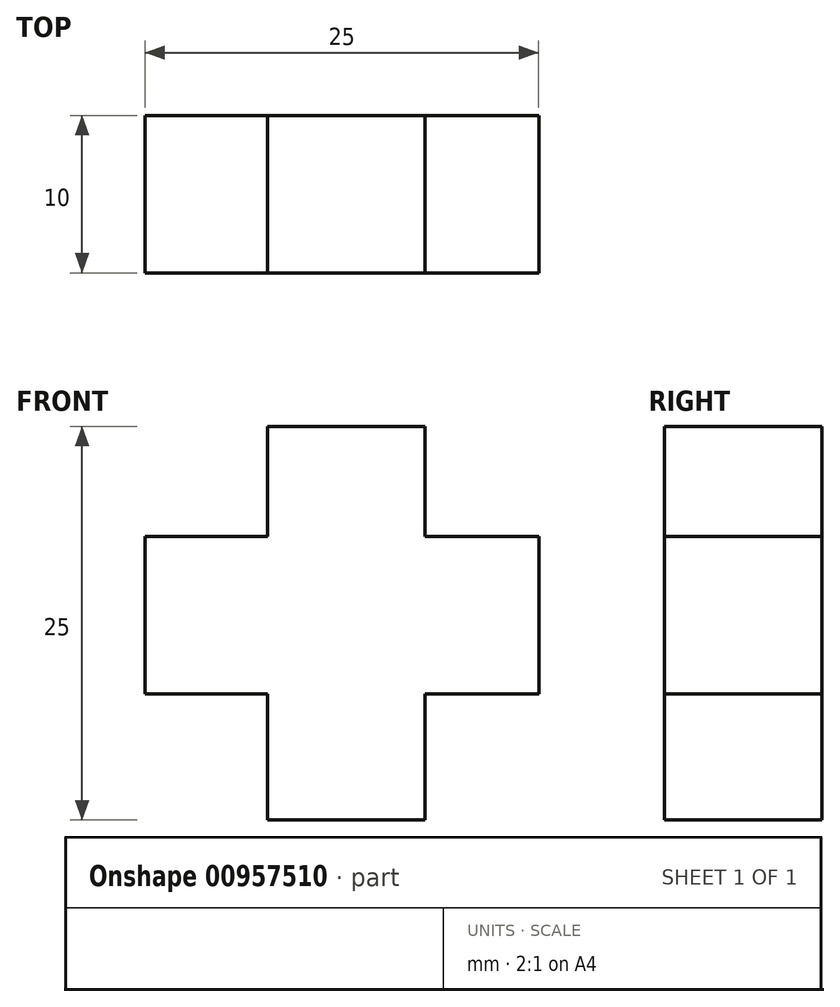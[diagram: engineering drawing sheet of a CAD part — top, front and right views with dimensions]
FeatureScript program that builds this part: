
annotation { "Feature Type Name" : "Feature", "Feature Type Description" : "" }
export const myFeature = defineFeature(function(context is Context, id is Id, definition is map)
    precondition{}
    {
        {
            var Q0;
            Q0=qCreatedBy(makeId("Front.planeOp"),FACE);
            var sketch = newSketch(context, id + "F0", { "sketchPlane" : qUnion([Q0])});
            skLineSegment(sketch, "E0.bottom", {"start": v(-11.23, 5.5) * mm, "end": v(13.77, 5.5) * mm});
            skLineSegment(sketch, "E0.top", {"start": v(-11.23, -4.5) * mm, "end": v(13.77, -4.5) * mm});
            skLineSegment(sketch, "E0.left", {"start": v(-11.23, 5.5) * mm, "end": v(-11.23, -4.5) * mm});
            skLineSegment(sketch, "E0.right", {"start": v(13.77, 5.5) * mm, "end": v(13.77, -4.5) * mm});
            skLineSegment(sketch, "E1", {"start": v(-11.23, -4.5) * mm, "end": v(-11.29, 0.5) * mm});
            skLineSegment(sketch, "E2.bottom", {"start": v(-3.46, 12.5) * mm, "end": v(6.54, 12.5) * mm});
            skLineSegment(sketch, "E2.top", {"start": v(-3.46, -12.5) * mm, "end": v(6.54, -12.5) * mm});
            skLineSegment(sketch, "E2.left", {"start": v(-3.46, 12.5) * mm, "end": v(-3.46, -12.5) * mm});
            skLineSegment(sketch, "E2.right", {"start": v(6.54, 12.5) * mm, "end": v(6.54, -12.5) * mm});
            skSolve(sketch);
        }
        {
            var Q0;
            Q0 = qSketchRegion(id + "F0", true);
            extrude(context, id + "F1", {"entities" : qUnion([Q0]), "depth" : 10 * mm, "offsetDistance" : 25 * mm});
        }
    });
